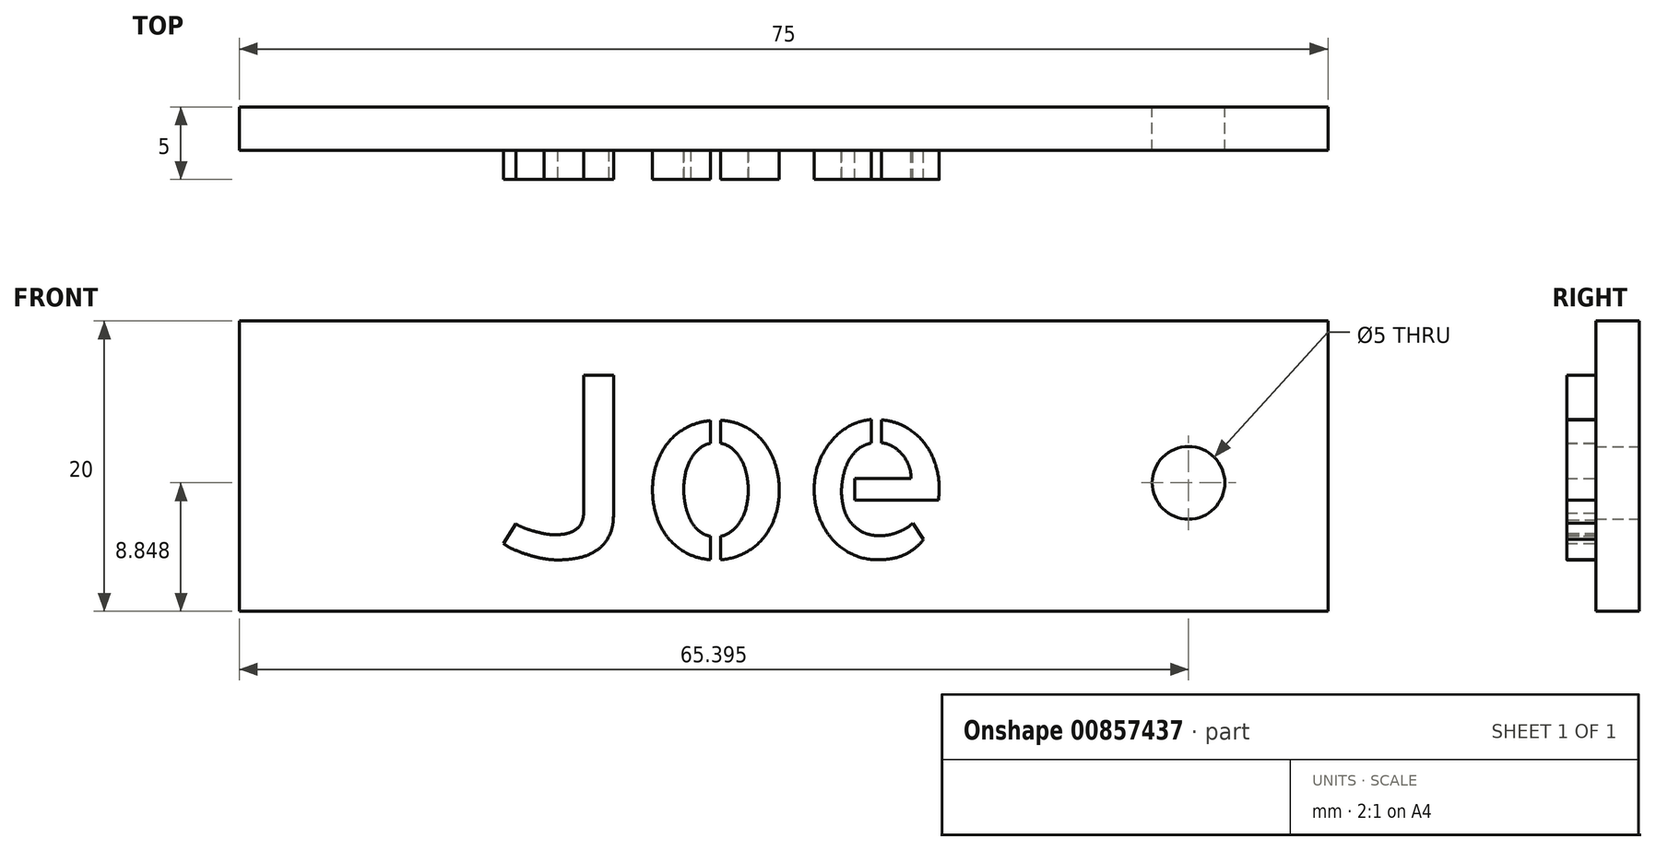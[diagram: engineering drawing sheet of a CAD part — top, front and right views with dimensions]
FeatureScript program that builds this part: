
annotation { "Feature Type Name" : "Feature", "Feature Type Description" : "" }
export const myFeature = defineFeature(function(context is Context, id is Id, definition is map)
    precondition{}
    {
        {
            var Q0;
            Q0=qCreatedBy(makeId("Front.planeOp"),FACE);
            var sketch = newSketch(context, id + "F0", { "sketchPlane" : qUnion([Q0])});
            skLineSegment(sketch, "E0.bottom", {"start": v(0, 0) * mm, "end": v(75, 0) * mm});
            skLineSegment(sketch, "E0.top", {"start": v(0, -20) * mm, "end": v(75, -20) * mm});
            skLineSegment(sketch, "E0.left", {"start": v(0, 0) * mm, "end": v(0, -20) * mm});
            skLineSegment(sketch, "E0.right", {"start": v(75, 0) * mm, "end": v(75, -20) * mm});
            skPoint(sketch, "E1.centerSnap0", {"position": v(37.5, 0) * mm});
            skCircle(sketch, "E2", {"center": v(65.4, -11.15) * mm, "radius": 2.5 * mm});
            skSolve(sketch);
        }
        {
            var Q0;
            Q0 = qSketchRegion(id + "F0", true);
            extrude(context, id + "F1", {"entities" : qUnion([Q0]), "depth" : 3 * mm, "offsetDistance" : 25 * mm});
        }
        {
            var Q0;
            Q0=makeQuery(id+"F1.opExtrude","CAP_FACE",FACE,{"disambiguationData":[OSD([sQuery(id+"F0.wireOp",EDGE,"E0.bottom"),sQuery(id+"F0.wireOp",EDGE,"E0.top"),sQuery(id+"F0.wireOp",EDGE,"E0.left"),sQuery(id+"F0.wireOp",EDGE,"E0.right"),sQuery(id+"F0.wireOp",EDGE,"E2")])],"isStart":false});
            var sketch = newSketch(context, id + "F2", { "sketchPlane" : qUnion([Q0])});
            skText(sketch, "E3", { "text": "Joe", "fontName": "AllertaStencil-Regular.ttf"});
            const initialGuessF2  = {"E3": [0.01776, -0.01638, 1, 0, 0.0124]};
            skSetInitialGuess(sketch, initialGuessF2);
            skSolve(sketch);
        }
        {
            var Q0;
            Q0 = qSketchRegion(id + "F2", true);
            extrude(context, id + "F3", {"entities" : qUnion([Q0]), "operationType" : NewBodyOperationType.ADD, "depth" : 2 * mm, "offsetDistance" : 25 * mm});
        }
    });
